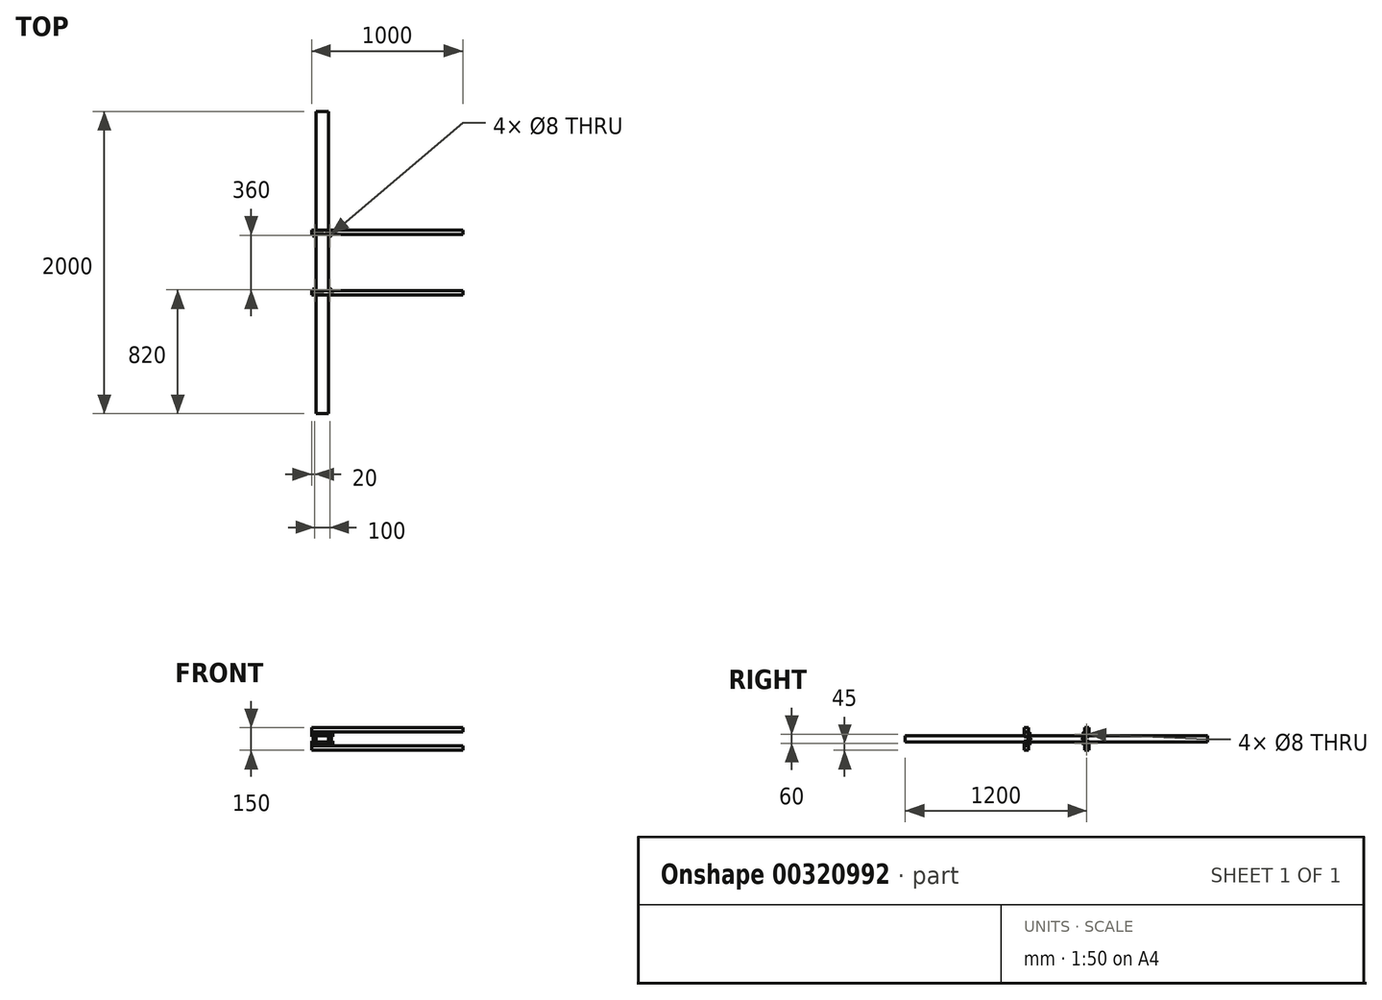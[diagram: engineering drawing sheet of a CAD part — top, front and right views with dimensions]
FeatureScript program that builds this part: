
annotation { "Feature Type Name" : "Feature", "Feature Type Description" : "" }
export const myFeature = defineFeature(function(context is Context, id is Id, definition is map)
    precondition{}
    {
        {
            var Q0;
            Q0=qCreatedBy(makeId("Front.planeOp"),FACE);
            var sketch = newSketch(context, id + "F0", { "sketchPlane" : qUnion([Q0])});
            skLineSegment(sketch, "E0.bottom", {"start": v(-40, 20) * mm, "end": v(40, 20) * mm});
            skLineSegment(sketch, "E0.top", {"start": v(-40, -20) * mm, "end": v(40, -20) * mm});
            skLineSegment(sketch, "E0.left", {"start": v(-40, 20) * mm, "end": v(-40, -20) * mm});
            skLineSegment(sketch, "E0.right", {"start": v(40, 20) * mm, "end": v(40, -20) * mm});
            skPoint(sketch, "E0.middle", {"position": v(0, 0) * mm});
            skSolve(sketch);
        }
        {
            var Q0;
            Q0=makeQuery(id+"F0.imprint","IMPRINT",FACE,{"disambiguationData":[TD([[makeQuery(id+"F0.imprint","IMPRINT",EDGE,{"derivedFrom":sQuery(id+"F0.wireOp",EDGE,"E0.bottom")}),-1.0]])]});
            extrude(context, id + "F1", {"entities" : qUnion([Q0]), "endBound" : BoundingType.SYMMETRIC, "depth" : 2000 * mm});
        }
        {
            var Q0;
            Q0=qCreatedBy(makeId("Right.planeOp"),FACE);
            var sketch = newSketch(context, id + "F2", { "sketchPlane" : qUnion([Q0])});
            skLineSegment(sketch, "E1", {"start": v(49.45, 30) * mm, "end": v(-36.57, 30) * mm, "construction": true});
            skCircle(sketch, "E2", {"center": v(200, 30) * mm, "radius": 10 * mm});
            skCircle(sketch, "E3", {"center": v(200, 30) * mm, "radius": 4 * mm});
            skCircle(sketch, "E4.MirrorC", {"center": v(-200, 30) * mm, "radius": 10 * mm});
            skCircle(sketch, "E5.MirrorC", {"center": v(-200, 30) * mm, "radius": 4 * mm});
            skSolve(sketch);
        }
        {
            var Q0;
            Q0=makeQuery(id+"F2.imprint","IMPRINT",FACE,{"disambiguationData":[TD([[makeQuery(id+"F2.imprint","IMPRINT",EDGE,{"derivedFrom":sQuery(id+"F2.wireOp",EDGE,"E2")}),1.0]])]});
            var Q1;
            Q1=makeQuery(id+"F2.imprint","IMPRINT",FACE,{"disambiguationData":[TD([[makeQuery(id+"F2.imprint","IMPRINT",EDGE,{"derivedFrom":sQuery(id+"F2.wireOp",EDGE,"E4.MirrorC")}),-1.0]])]});
            extrude(context, id + "F3", {"entities" : qUnion([Q0, Q1]), "operationType" : NewBodyOperationType.ADD, "depth" : 8 * mm});
        }
        {
            var Q0;
            Q0=makeQuery(id+"F3.opExtrude","CAP_FACE",FACE,{"disambiguationData":[OSD([sQuery(id+"F2.wireOp",EDGE,"E2"),sQuery(id+"F2.wireOp",EDGE,"E3")])],"isStart":true});
            var sketch = newSketch(context, id + "F4", { "sketchPlane" : qUnion([Q0])});
            skCircle(sketch, "E6.0", {"center": v(-200, 30) * mm, "radius": 4 * mm});
            skCircle(sketch, "E7.0", {"center": v(200, 30) * mm, "radius": 4 * mm});
            skSolve(sketch);
        }
        {
            var Q0;
            Q0=makeQuery(id+"F4.imprint","IMPRINT",FACE,{"disambiguationData":[TD([[makeQuery(id+"F4.imprint","IMPRINT",EDGE,{"derivedFrom":sQuery(id+"F4.wireOp",EDGE,"E6.0")}),-1.0]])]});
            var Q1;
            Q1=makeQuery(id+"F4.imprint","IMPRINT",FACE,{"disambiguationData":[TD([[makeQuery(id+"F4.imprint","IMPRINT",EDGE,{"derivedFrom":sQuery(id+"F4.wireOp",EDGE,"E7.0")}),1.0]])]});
            extrude(context, id + "F5", {"entities" : qUnion([Q0, Q1]), "endBound" : BoundingType.SYMMETRIC, "depth" : 140 * mm});
        }
        {
            var Q0;
            Q0=makeQuery(id+"F3.opExtrude","SWEPT_BODY",BODY,{"disambiguationData":[OSD([sQuery(id+"F2.wireOp",EDGE,"E4.MirrorC"),sQuery(id+"F2.wireOp",EDGE,"E5.MirrorC")])]});
            var Q1;
            Q1=makeQuery(id+"F3.opExtrude","SWEPT_BODY",BODY,{"disambiguationData":[OSD([sQuery(id+"F2.wireOp",EDGE,"E2"),sQuery(id+"F2.wireOp",EDGE,"E3")])]});
            transform(context, id + "F6", {"entities" : qUnion([Q0, Q1]), "transformType" : TransformType.TRANSLATION_3D, "dx" : 25 * mm, "dy" : 0 * mm, "dz" : 0 * mm, "makeCopy" : false});
        }
        {
            var Q0;
            Q0=makeQuery(id+"F3.opExtrude","SWEPT_BODY",BODY,{"disambiguationData":[OSD([sQuery(id+"F2.wireOp",EDGE,"E2"),sQuery(id+"F2.wireOp",EDGE,"E3")])]});
            var Q1;
            Q1=makeQuery(id+"F3.opExtrude","SWEPT_BODY",BODY,{"disambiguationData":[OSD([sQuery(id+"F2.wireOp",EDGE,"E4.MirrorC"),sQuery(id+"F2.wireOp",EDGE,"E5.MirrorC")])]});
            var Q2;
            Q2=qCreatedBy(makeId("Right.planeOp"),FACE);
            mirror(context, id + "F7", {"entities" : qUnion([Q0, Q1]), "mirrorPlane" : qUnion([Q2])});
        }
        {
            var Q0;
            Q0=makeQuery(id+"F5.opExtrude","SWEPT_BODY",BODY,{"disambiguationData":[OSD([sQuery(id+"F4.wireOp",EDGE,"E6.0")])]});
            var Q1;
            Q1=makeQuery(id+"F7.opPattern","COPY",BODY,{"derivedFrom":makeQuery(id+"F3.opExtrude","SWEPT_BODY",BODY,{"disambiguationData":[OSD([sQuery(id+"F2.wireOp",EDGE,"E2"),sQuery(id+"F2.wireOp",EDGE,"E3")])]}),"instanceName":"1"});
            var Q2;
            Q2=makeQuery(id+"F3.opExtrude","SWEPT_BODY",BODY,{"disambiguationData":[OSD([sQuery(id+"F2.wireOp",EDGE,"E2"),sQuery(id+"F2.wireOp",EDGE,"E3")])]});
            var Q3;
            Q3=makeQuery(id+"F5.opExtrude","SWEPT_BODY",BODY,{"disambiguationData":[OSD([sQuery(id+"F4.wireOp",EDGE,"E7.0")])]});
            var Q4;
            Q4=makeQuery(id+"F7.opPattern","COPY",BODY,{"derivedFrom":makeQuery(id+"F3.opExtrude","SWEPT_BODY",BODY,{"disambiguationData":[OSD([sQuery(id+"F2.wireOp",EDGE,"E4.MirrorC"),sQuery(id+"F2.wireOp",EDGE,"E5.MirrorC")])]}),"instanceName":"1"});
            var Q5;
            Q5=makeQuery(id+"F3.opExtrude","SWEPT_BODY",BODY,{"disambiguationData":[OSD([sQuery(id+"F2.wireOp",EDGE,"E4.MirrorC"),sQuery(id+"F2.wireOp",EDGE,"E5.MirrorC")])]});
            var Q6;
            Q6=qCreatedBy(makeId("Top.planeOp"),FACE);
            mirror(context, id + "F8", {"operationType" : NewBodyOperationType.ADD, "entities" : qUnion([Q0, Q1, Q2, Q3, Q4, Q5]), "mirrorPlane" : qUnion([Q6])});
        }
        {
            var Q0;
            Q0=makeQuery(id+"F7.opPattern","COPY",BODY,{"derivedFrom":makeQuery(id+"F3.opExtrude","SWEPT_BODY",BODY,{"disambiguationData":[OSD([sQuery(id+"F2.wireOp",EDGE,"E2"),sQuery(id+"F2.wireOp",EDGE,"E3")])]}),"instanceName":"1"});
            var Q1;
            Q1=makeQuery(id+"F1.opExtrude","SWEPT_EDGE",EDGE,{"disambiguationData":[OSD([sQuery(id+"F0.wireOp",EDGE,"E0.bottom"),sQuery(id+"F0.wireOp",EDGE,"E0.left")])]});
            transform(context, id + "F9", {"entities" : qUnion([Q0]), "transformType" : TransformType.ROTATION, "transformAxis" : qUnion([Q1]), "angle" : 90 * degree, "makeCopy" : true});
        }
        {
            var Q0;
            Q0=makeQuery(id+"F9.opPattern","COPY",BODY,{"derivedFrom":makeQuery(id+"F7.opPattern","COPY",BODY,{"derivedFrom":makeQuery(id+"F3.opExtrude","SWEPT_BODY",BODY,{"disambiguationData":[OSD([sQuery(id+"F2.wireOp",EDGE,"E2"),sQuery(id+"F2.wireOp",EDGE,"E3")])]}),"instanceName":"1"}),"instanceName":"1"});
            var Q1;
            Q1=makeQuery(id+"F5.opExtrude","SWEPT_FACE",FACE,{"disambiguationData":[OSD([sQuery(id+"F4.wireOp",EDGE,"E6.0")])]});
            transform(context, id + "F10", {"entities" : qUnion([Q0]), "transformType" : TransformType.TRANSLATION_DISTANCE, "transformDirection" : qUnion([Q1]), "distance" : 25 * mm, "oppositeDirection" : true, "makeCopy" : false});
        }
        {
            var Q0;
            Q0=makeQuery(id+"F9.opPattern","COPY",BODY,{"derivedFrom":makeQuery(id+"F7.opPattern","COPY",BODY,{"derivedFrom":makeQuery(id+"F3.opExtrude","SWEPT_BODY",BODY,{"disambiguationData":[OSD([sQuery(id+"F2.wireOp",EDGE,"E2"),sQuery(id+"F2.wireOp",EDGE,"E3")])]}),"instanceName":"1"}),"instanceName":"1"});
            var Q1;
            Q1=makeQuery(id+"F1.opExtrude","SWEPT_EDGE",EDGE,{"disambiguationData":[OSD([sQuery(id+"F0.wireOp",EDGE,"E0.bottom"),sQuery(id+"F0.wireOp",EDGE,"E0.left")])]});
            transform(context, id + "F11", {"entities" : qUnion([Q0]), "transformType" : TransformType.TRANSLATION_DISTANCE, "transformDirection" : qUnion([Q1]), "distance" : 20 * mm, "oppositeDirection" : true, "makeCopy" : false});
        }
        {
            var Q0;
            Q0=makeQuery(id+"F9.opPattern","COPY",BODY,{"derivedFrom":makeQuery(id+"F7.opPattern","COPY",BODY,{"derivedFrom":makeQuery(id+"F3.opExtrude","SWEPT_BODY",BODY,{"disambiguationData":[OSD([sQuery(id+"F2.wireOp",EDGE,"E2"),sQuery(id+"F2.wireOp",EDGE,"E3")])]}),"instanceName":"1"}),"instanceName":"1"});
            var Q1;
            Q1=makeQuery(id+"F5.opExtrude","SWEPT_FACE",FACE,{"disambiguationData":[OSD([sQuery(id+"F4.wireOp",EDGE,"E6.0")])]});
            transform(context, id + "F12", {"entities" : qUnion([Q0]), "transformType" : TransformType.TRANSLATION_DISTANCE, "transformDirection" : qUnion([Q1]), "distance" : 5 * mm, "makeCopy" : false});
        }
        {
            var Q0;
            Q0=makeQuery(id+"F9.opPattern","COPY",FACE,{"derivedFrom":makeQuery(id+"F7.opPattern","COPY",FACE,{"derivedFrom":makeQuery(id+"F3.opExtrude","CAP_FACE",FACE,{"disambiguationData":[OSD([sQuery(id+"F2.wireOp",EDGE,"E2"),sQuery(id+"F2.wireOp",EDGE,"E3")])],"isStart":false}),"instanceName":"1"}),"instanceName":"1"});
            var sketch = newSketch(context, id + "F13", { "sketchPlane" : qUnion([Q0])});
            skCircle(sketch, "E8.0.0", {"center": v(-50, 180) * mm, "radius": 10 * mm});
            skSolve(sketch);
        }
        {
            var Q0;
            Q0=makeQuery(id+"F13.imprint","IMPRINT",FACE,{"disambiguationData":[TD([[makeQuery(id+"F13.imprint","IMPRINT",EDGE,{"derivedFrom":makeQuery(id+"F9.opPattern","COPY",EDGE,{"derivedFrom":makeQuery(id+"F7.opPattern","COPY",EDGE,{"derivedFrom":makeQuery(id+"F3.opExtrude","CAP_EDGE",EDGE,{"disambiguationData":[OSD([sQuery(id+"F2.wireOp",EDGE,"E3")])],"isStart":false}),"instanceName":"1"}),"instanceName":"1"})}),-1.0]])]});
            extrude(context, id + "F14", {"entities" : qUnion([Q0]), "endBound" : BoundingType.SYMMETRIC, "depth" : 80 * mm});
        }
        {
            var Q0;
            Q0=makeQuery(id+"F14.opExtrude","SWEPT_BODY",BODY,{"disambiguationData":[OSD([sQuery(id+"F2.wireOp",EDGE,"E3")])]});
            var Q1;
            Q1=makeQuery(id+"F14.opExtrude","SWEPT_FACE",FACE,{"disambiguationData":[OSD([sQuery(id+"F2.wireOp",EDGE,"E3")])]});
            transform(context, id + "F15", {"entities" : qUnion([Q0]), "transformType" : TransformType.TRANSLATION_DISTANCE, "transformDirection" : qUnion([Q1]), "distance" : 11 * mm, "makeCopy" : false});
        }
        {
            var Q0;
            Q0=makeQuery(id+"F9.opPattern","COPY",BODY,{"derivedFrom":makeQuery(id+"F7.opPattern","COPY",BODY,{"derivedFrom":makeQuery(id+"F3.opExtrude","SWEPT_BODY",BODY,{"disambiguationData":[OSD([sQuery(id+"F2.wireOp",EDGE,"E2"),sQuery(id+"F2.wireOp",EDGE,"E3")])]}),"instanceName":"1"}),"instanceName":"1"});
            var Q1;
            Q1=makeQuery(id+"F14.opExtrude","SWEPT_FACE",FACE,{"disambiguationData":[OSD([sQuery(id+"F2.wireOp",EDGE,"E3")])]});
            transform(context, id + "F16", {"entities" : qUnion([Q0]), "transformType" : TransformType.TRANSLATION_DISTANCE, "transformDirection" : qUnion([Q1]), "distance" : 8 * mm, "makeCopy" : false});
        }
        {
            var Q0;
            Q0=makeQuery(id+"F9.opPattern","COPY",BODY,{"derivedFrom":makeQuery(id+"F7.opPattern","COPY",BODY,{"derivedFrom":makeQuery(id+"F3.opExtrude","SWEPT_BODY",BODY,{"disambiguationData":[OSD([sQuery(id+"F2.wireOp",EDGE,"E2"),sQuery(id+"F2.wireOp",EDGE,"E3")])]}),"instanceName":"1"}),"instanceName":"1"});
            var Q1;
            Q1=makeQuery(id+"F14.opExtrude","SWEPT_BODY",BODY,{"disambiguationData":[OSD([sQuery(id+"F2.wireOp",EDGE,"E3")])]});
            var Q2;
            Q2=qCreatedBy(makeId("Front.planeOp"),FACE);
            mirror(context, id + "F17", {"operationType" : NewBodyOperationType.ADD, "entities" : qUnion([Q0, Q1]), "mirrorPlane" : qUnion([Q2])});
        }
        {
            var Q0;
            Q0=makeQuery(id+"F9.opPattern","COPY",BODY,{"derivedFrom":makeQuery(id+"F7.opPattern","COPY",BODY,{"derivedFrom":makeQuery(id+"F3.opExtrude","SWEPT_BODY",BODY,{"disambiguationData":[OSD([sQuery(id+"F2.wireOp",EDGE,"E2"),sQuery(id+"F2.wireOp",EDGE,"E3")])]}),"instanceName":"1"}),"instanceName":"1"});
            var Q1;
            Q1=makeQuery(id+"F14.opExtrude","SWEPT_BODY",BODY,{"disambiguationData":[OSD([sQuery(id+"F2.wireOp",EDGE,"E3")])]});
            var Q2;
            Q2=makeQuery(id+"F17.opPattern","COPY",BODY,{"derivedFrom":makeQuery(id+"F14.opExtrude","SWEPT_BODY",BODY,{"disambiguationData":[OSD([sQuery(id+"F2.wireOp",EDGE,"E3")])]}),"instanceName":"1"});
            var Q3;
            Q3=makeQuery(id+"F17.opPattern","COPY",BODY,{"derivedFrom":makeQuery(id+"F9.opPattern","COPY",BODY,{"derivedFrom":makeQuery(id+"F7.opPattern","COPY",BODY,{"derivedFrom":makeQuery(id+"F3.opExtrude","SWEPT_BODY",BODY,{"disambiguationData":[OSD([sQuery(id+"F2.wireOp",EDGE,"E2"),sQuery(id+"F2.wireOp",EDGE,"E3")])]}),"instanceName":"1"}),"instanceName":"1"}),"instanceName":"1"});
            var Q4;
            Q4=qCreatedBy(makeId("Right.planeOp"),FACE);
            mirror(context, id + "F18", {"operationType" : NewBodyOperationType.ADD, "entities" : qUnion([Q0, Q1, Q2, Q3]), "mirrorPlane" : qUnion([Q4])});
        }
        {
            var Q0;
            Q0=makeQuery(id+"F5.opExtrude","CAP_FACE",FACE,{"disambiguationData":[OSD([sQuery(id+"F4.wireOp",EDGE,"E7.0")])],"isStart":true});
            var sketch = newSketch(context, id + "F19", { "sketchPlane" : qUnion([Q0])});
            skCircle(sketch, "E9.0", {"center": v(-200, 30) * mm, "radius": 4 * mm});
            skLineSegment(sketch, "E10.bottom", {"start": v(-215, 45) * mm, "end": v(-185, 45) * mm});
            skLineSegment(sketch, "E10.top", {"start": v(-215, 15) * mm, "end": v(-185, 15) * mm});
            skLineSegment(sketch, "E10.left", {"start": v(-215, 45) * mm, "end": v(-215, 15) * mm});
            skLineSegment(sketch, "E10.right", {"start": v(-185, 45) * mm, "end": v(-185, 15) * mm});
            skSolve(sketch);
        }
        {
            var Q0;
            Q0=makeQuery(id+"F19.imprint","IMPRINT",FACE,{"disambiguationData":[TD([[makeQuery(id+"F19.imprint","IMPRINT",EDGE,{"derivedFrom":sQuery(id+"F19.wireOp",EDGE,"E9.0")}),1.0]])]});
            extrude(context, id + "F20", {"entities" : qUnion([Q0]), "oppositeDirection" : true, "depth" : 5 * mm});
        }
        {
            var Q0;
            Q0=makeQuery(id+"F20.opExtrude","SWEPT_FACE",FACE,{"disambiguationData":[OSD([sQuery(id+"F19.wireOp",EDGE,"E10.bottom")])]});
            var sketch = newSketch(context, id + "F21", { "sketchPlane" : qUnion([Q0])});
            skLineSegment(sketch, "E11.0.0", {"start": v(70, -215) * mm, "end": v(70, -185) * mm});
            skLineSegment(sketch, "E11.0.1", {"start": v(70, -185) * mm, "end": v(65, -185) * mm});
            skLineSegment(sketch, "E11.0.2", {"start": v(65, -185) * mm, "end": v(65, -215) * mm});
            skLineSegment(sketch, "E11.0.3", {"start": v(65, -215) * mm, "end": v(70, -215) * mm});
            skLineSegment(sketch, "E12.bottom", {"start": v(65, -185) * mm, "end": v(40, -185) * mm});
            skLineSegment(sketch, "E12.top", {"start": v(65, -215) * mm, "end": v(40, -215) * mm});
            skLineSegment(sketch, "E12.right", {"start": v(40, -185) * mm, "end": v(40, -215) * mm});
            skSolve(sketch);
        }
        {
            var Q0;
            Q0=makeQuery(id+"F21.imprint","IMPRINT",FACE,{"disambiguationData":[TD([[makeQuery(id+"F21.imprint","IMPRINT",EDGE,{"derivedFrom":sQuery(id+"F21.wireOp",EDGE,"E12.bottom")}),1.0]])]});
            extrude(context, id + "F22", {"entities" : qUnion([Q0]), "operationType" : NewBodyOperationType.ADD, "oppositeDirection" : true, "depth" : 5 * mm});
        }
        {
            var Q0;
            Q0=makeQuery(id+"F20.opExtrude","SWEPT_BODY",BODY,{"disambiguationData":[OSD([sQuery(id+"F19.wireOp",EDGE,"E9.0"),sQuery(id+"F19.wireOp",EDGE,"E10.bottom"),sQuery(id+"F19.wireOp",EDGE,"E10.top"),sQuery(id+"F19.wireOp",EDGE,"E10.left"),sQuery(id+"F19.wireOp",EDGE,"E10.right")])]});
            var Q1;
            Q1=qCreatedBy(makeId("Right.planeOp"),FACE);
            mirror(context, id + "F23", {"operationType" : NewBodyOperationType.ADD, "entities" : qUnion([Q0]), "mirrorPlane" : qUnion([Q1])});
        }
        {
            var Q0;
            Q0=makeQuery(id+"F5.opExtrude","SWEPT_BODY",BODY,{"disambiguationData":[OSD([sQuery(id+"F4.wireOp",EDGE,"E7.0")])]});
            var Q1;
            Q1=qCreatedBy(makeId("Front.planeOp"),FACE);
            mirror(context, id + "F24", {"entities" : qUnion([Q0]), "mirrorPlane" : qUnion([Q1])});
        }
        {
            var Q0;
            Q0=makeQuery(id+"F5.opExtrude","SWEPT_BODY",BODY,{"disambiguationData":[OSD([sQuery(id+"F4.wireOp",EDGE,"E7.0")])]});
            var Q1;
            Q1=makeQuery(id+"F24.opPattern","COPY",BODY,{"derivedFrom":makeQuery(id+"F5.opExtrude","SWEPT_BODY",BODY,{"disambiguationData":[OSD([sQuery(id+"F4.wireOp",EDGE,"E7.0")])]}),"instanceName":"1"});
            var Q2;
            Q2=qCreatedBy(makeId("Top.planeOp"),FACE);
            mirror(context, id + "F25", {"entities" : qUnion([Q0, Q1]), "mirrorPlane" : qUnion([Q2])});
        }
        {
            var Q0;
            Q0=makeQuery(id+"F24.opPattern","COPY",FACE,{"derivedFrom":makeQuery(id+"F23.boolean.opBoolean","MERGE",FACE,{"derivedFrom":[makeQuery(id+"F5.opExtrude","CAP_FACE",FACE,{"disambiguationData":[OSD([sQuery(id+"F4.wireOp",EDGE,"E7.0")])],"isStart":false}),makeQuery(id+"F23.opPattern","COPY",FACE,{"derivedFrom":makeQuery(id+"F20.opExtrude","CAP_FACE",FACE,{"disambiguationData":[OSD([sQuery(id+"F19.wireOp",EDGE,"E9.0"),sQuery(id+"F19.wireOp",EDGE,"E10.bottom"),sQuery(id+"F19.wireOp",EDGE,"E10.top"),sQuery(id+"F19.wireOp",EDGE,"E10.left"),sQuery(id+"F19.wireOp",EDGE,"E10.right")])],"isStart":true}),"instanceName":"1"})]}),"instanceName":"1"});
            var sketch = newSketch(context, id + "F26", { "sketchPlane" : qUnion([Q0])});
            skLineSegment(sketch, "E13.0.0", {"start": v(-215, 45) * mm, "end": v(-215, 15) * mm});
            skLineSegment(sketch, "E13.0.1", {"start": v(-215, 15) * mm, "end": v(-185, 15) * mm});
            skLineSegment(sketch, "E13.0.2", {"start": v(-185, 15) * mm, "end": v(-185, 45) * mm});
            skLineSegment(sketch, "E13.0.3", {"start": v(-185, 45) * mm, "end": v(-215, 45) * mm});
            skLineSegment(sketch, "E14.top", {"start": v(-185, 75) * mm, "end": v(-215, 75) * mm});
            skLineSegment(sketch, "E14.left", {"start": v(-185, 45) * mm, "end": v(-185, 75) * mm});
            skLineSegment(sketch, "E14.right", {"start": v(-215, 45) * mm, "end": v(-215, 75) * mm});
            skSolve(sketch);
        }
        {
            var Q0;
            Q0=makeQuery(id+"F26.imprint","IMPRINT",FACE,{"disambiguationData":[TD([[makeQuery(id+"F26.imprint","IMPRINT",EDGE,{"derivedFrom":sQuery(id+"F26.wireOp",EDGE,"E13.0.3")}),1.0]])]});
            extrude(context, id + "F27", {"entities" : qUnion([Q0]), "oppositeDirection" : true, "depth" : 1000 * mm});
        }
        {
            var Q0;
            Q0=makeQuery(id+"F27.opExtrude","SWEPT_BODY",BODY,{"disambiguationData":[OSD([sQuery(id+"F26.wireOp",EDGE,"E13.0.3"),sQuery(id+"F26.wireOp",EDGE,"E14.top"),sQuery(id+"F26.wireOp",EDGE,"E14.left"),sQuery(id+"F26.wireOp",EDGE,"E14.right")])]});
            var Q1;
            Q1=qCreatedBy(makeId("Top.planeOp"),FACE);
            mirror(context, id + "F28", {"entities" : qUnion([Q0]), "mirrorPlane" : qUnion([Q1])});
        }
        {
            var Q0;
            Q0=makeQuery(id+"F27.opExtrude","SWEPT_BODY",BODY,{"disambiguationData":[OSD([sQuery(id+"F26.wireOp",EDGE,"E13.0.3"),sQuery(id+"F26.wireOp",EDGE,"E14.top"),sQuery(id+"F26.wireOp",EDGE,"E14.left"),sQuery(id+"F26.wireOp",EDGE,"E14.right")])]});
            var Q1;
            Q1=makeQuery(id+"F28.opPattern","COPY",BODY,{"derivedFrom":makeQuery(id+"F27.opExtrude","SWEPT_BODY",BODY,{"disambiguationData":[OSD([sQuery(id+"F26.wireOp",EDGE,"E13.0.3"),sQuery(id+"F26.wireOp",EDGE,"E14.top"),sQuery(id+"F26.wireOp",EDGE,"E14.left"),sQuery(id+"F26.wireOp",EDGE,"E14.right")])]}),"instanceName":"1"});
            var Q2;
            Q2=qCreatedBy(makeId("Front.planeOp"),FACE);
            mirror(context, id + "F29", {"entities" : qUnion([Q0, Q1]), "mirrorPlane" : qUnion([Q2])});
        }
    });
